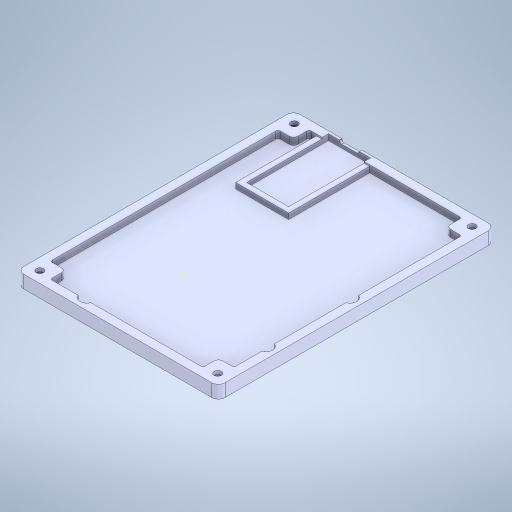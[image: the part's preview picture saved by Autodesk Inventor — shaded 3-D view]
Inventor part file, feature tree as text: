
AUTODESK INVENTOR PART (.ipt)
format: ipt  version: 2024 (Build 280153020, 153B)  size: 477,696 bytes
history: native  units: in
note: dims shown in document units (in); Inventor stores cm internally (conversion verified against a paired STEP export)
features: move_body x7, sketch x6, direct_edit x5, extrude x5, other x5
ambient origin geometry x8: Origin, YZ Plane, XZ Plane, XY Plane, X Axis, Y Axis, Z Axis, Center Point
bodies: Solid1 (feature_tree)
feature tree (28):
  sketch  "Sketch1"  dims[d6=0.0in d7=0.0in d8=0.03in d9=0.0in d10=0.0in d11=-0.03in]
  direct_edit  "Direct Edit1"
  direct_edit  "Direct Edit2"
  direct_edit  "Direct Edit3"
  direct_edit  "Direct Edit4"
  direct_edit  "Direct Edit5"
  extrude  "Extrusion1"  TaperAngle=0.0deg  [1 undecoded]
  extrude  "Extrusion2"  Depth=0.015in TaperAngle=0.0deg
  extrude  "Extrusion3"  TaperAngle=0.0deg  [1 undecoded]
  extrude  "Extrusion4"  [1 undecoded]
  extrude  "Extrusion5"  [1 undecoded]
  sketch  "Sketch3"  dims[d12=0.015in d13=0.0in d14=0.0in d15=0.015in d16=0.0in d17=0.0in]
  sketch  "Sketch4"  dims[d18=0.0in d19=0.0in d20=0.1378in d21=0.0in d22=0.0in d23=-0.1378in]
  sketch  "Sketch5"  dims[d24=0.0in d25=0.0in d26=0.0197in d27=-0.0394in]
  sketch  "Sketch6"  dims[d28=-0.0394in d29=-0.0394in]
  sketch  "Sketch7"  dims[d30=-0.0394in d31=4.9175in d32=0.0in d33=3.5807in d34=0.0in d35=0.2283in d36=0.0in d37=0.2362in d38=0.0in d39=0.1654in d40=0.0in]
  other  "Taglio-Estrusione5"
  move_body  "Move1"
  move_body  "Move2"
  move_body  "Move3"
  move_body  "Move4"
  move_body  "Move5"
  move_body  "Move6"
  move_body  "Move7"
  other  "Size1"
  other  "Size2"
  other  "Size3"
  other  "Size4"
note: 4 required parameter values undecoded (feature->parameter linkage not recoverable at this tier; creation-order binding heuristic only, values carry confidence <= 0.55)
